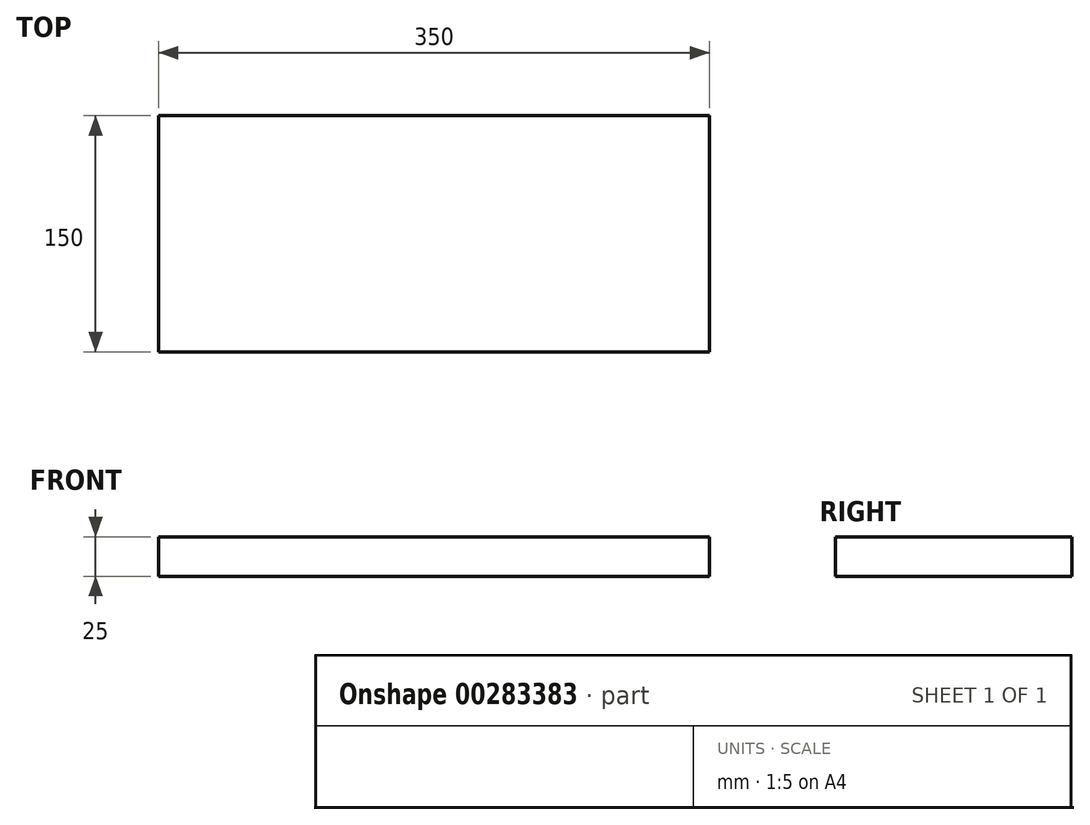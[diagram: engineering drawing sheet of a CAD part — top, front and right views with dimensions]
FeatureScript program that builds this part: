
annotation { "Feature Type Name" : "Feature", "Feature Type Description" : "" }
export const myFeature = defineFeature(function(context is Context, id is Id, definition is map)
    precondition{}
    {
        {
            var Q0;
            Q0=qCreatedBy(makeId("Top.planeOp"),FACE);
            var sketch = newSketch(context, id + "F0", { "sketchPlane" : qUnion([Q0])});
            skLineSegment(sketch, "E0.bottom", {"start": v(175, 75) * mm, "end": v(-175, 75) * mm});
            skLineSegment(sketch, "E0.top", {"start": v(175, -75) * mm, "end": v(-175, -75) * mm});
            skLineSegment(sketch, "E0.left", {"start": v(175, 75) * mm, "end": v(175, -75) * mm});
            skLineSegment(sketch, "E0.right", {"start": v(-175, 75) * mm, "end": v(-175, -75) * mm});
            skPoint(sketch, "E0.middle", {"position": v(0, 0) * mm});
            skSolve(sketch);
        }
        {
            var Q0;
            Q0 = qSketchRegion(id + "F0", true);
            var Q1;
            Q1=makeQuery(id+"F0.imprint","IMPRINT",FACE,{"disambiguationData":[TD([[makeQuery(id+"F0.imprint","IMPRINT",EDGE,{"derivedFrom":sQuery(id+"F0.wireOp",EDGE,"E0.bottom")}),1.0]])]});
            extrude(context, id + "F1", {"entities" : qUnion([Q0, Q1]), "depth" : 25 * mm});
        }
    });
